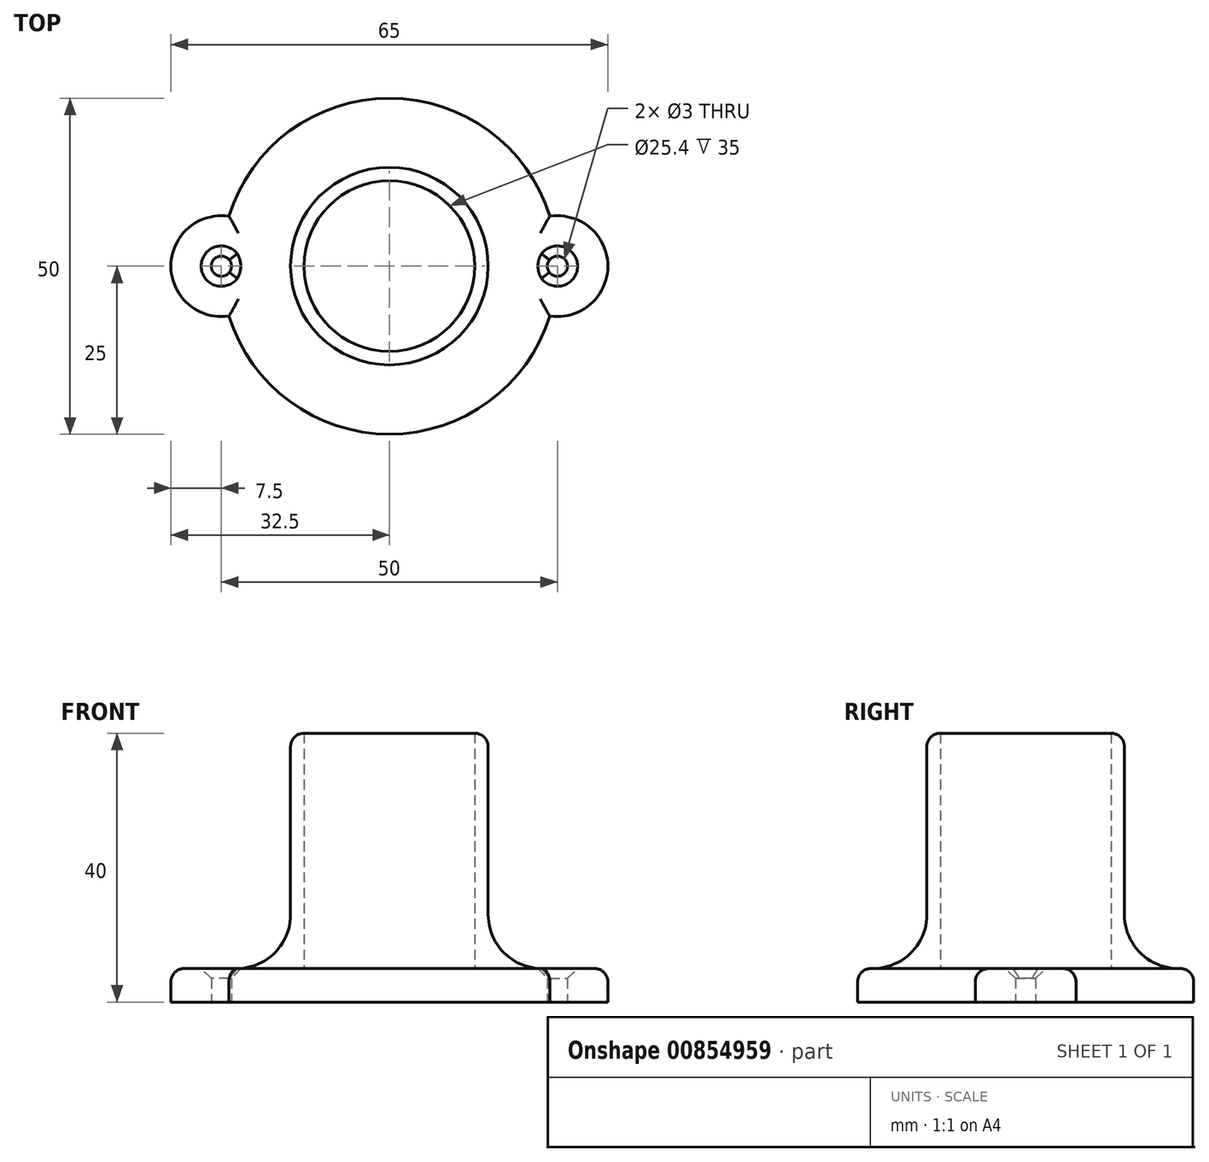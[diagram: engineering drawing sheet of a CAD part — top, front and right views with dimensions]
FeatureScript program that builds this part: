
annotation { "Feature Type Name" : "Feature", "Feature Type Description" : "" }
export const myFeature = defineFeature(function(context is Context, id is Id, definition is map)
    precondition{}
    {
        {
            var Q0;
            Q0=qCreatedBy(makeId("Top.planeOp"),FACE);
            var sketch = newSketch(context, id + "F0", { "sketchPlane" : qUnion([Q0])});
            skCircle(sketch, "E0", {"center": v(0, 0) * mm, "radius": 12.7 * mm});
            skCircle(sketch, "E1", {"center": v(0, 0) * mm, "radius": 11 * mm});
            skCircle(sketch, "E2", {"center": v(0, 0) * mm, "radius": 9 * mm});
            skCircle(sketch, "E3", {"center": v(0, 0) * mm, "radius": 14.7 * mm});
            skSolve(sketch);
        }
        {
            var Q0;
            Q0 = qSketchRegion(id + "F0", true);
            extrude(context, id + "F1", {"entities" : qUnion([Q0]), "depth" : 40 * mm, "offsetDistance" : 25 * mm});
        }
        {
            var Q0;
            Q0=qCreatedBy(makeId("Top.planeOp"),FACE);
            var sketch = newSketch(context, id + "F2", { "sketchPlane" : qUnion([Q0])});
            skCircle(sketch, "E4", {"center": v(0.24, -0.03) * mm, "radius": 11 * mm});
            skCircle(sketch, "E5", {"center": v(0.24, -0.03) * mm, "radius": 9 * mm});
            skSolve(sketch);
        }
        {
            var Q0;
            Q0=qCreatedBy(makeId("Top.planeOp"),FACE);
            var sketch = newSketch(context, id + "F3", { "sketchPlane" : qUnion([Q0])});
            skArc(sketch, "E6", {"start": v(-23.88, -7.42) * mm, "mid": v(0, -25) * mm, "end": v(23.88, -7.42) * mm});
            skArc(sketch, "E7", {"start": v(-23.88, 7.42) * mm, "mid": v(-32.5, 0) * mm, "end": v(-23.88, -7.42) * mm});
            skArc(sketch, "E8", {"start": v(23.88, -7.42) * mm, "mid": v(32.5, 0) * mm, "end": v(23.88, 7.42) * mm});
            skArc(sketch, "E9.trimOffspring", {"start": v(23.88, 7.42) * mm, "mid": v(0, 25) * mm, "end": v(-23.88, 7.42) * mm});
            skCircle(sketch, "E10", {"center": v(-25, 0) * mm, "radius": 1.5 * mm});
            skCircle(sketch, "E11", {"center": v(25, 0) * mm, "radius": 1.5 * mm});
            skSolve(sketch);
        }
        {
            var Q0;
            Q0 = qSketchRegion(id + "F3", true);
            extrude(context, id + "F4", {"entities" : qUnion([Q0]), "depth" : 5 * mm, "offsetDistance" : 25 * mm});
        }
        {
            var Q0;
            Q0=makeQuery(id+"F1.opExtrude","CAP_EDGE",EDGE,{"disambiguationData":[OSD([sQuery(id+"F0.wireOp",EDGE,"E3")])],"isStart":false});
            fillet(context, id + "F5", {"entities" : qUnion([Q0]), "radius" : 2 * mm, "tangentPropagation" : true, "allowEdgeOverflow" : false});
        }
        {
            var Q0;
            Q0=makeQuery(id+"F1.opExtrude","SWEPT_BODY",BODY,{"disambiguationData":[OSD([sQuery(id+"F0.wireOp",EDGE,"E0"),sQuery(id+"F0.wireOp",EDGE,"E3")])]});
            var Q1;
            Q1=makeQuery(id+"F3QXxj1bhoaXKLj_1.opExtrude","SWEPT_BODY",BODY,{"disambiguationData":[OSD([sQuery(id+"F2.wireOp",EDGE,"E4"),sQuery(id+"F2.wireOp",EDGE,"E5")])]});
            var Q2;
            Q2=makeQuery(id+"F4.opExtrude","SWEPT_BODY",BODY,{"disambiguationData":[OSD([sQuery(id+"F3.wireOp",EDGE,"E6"),sQuery(id+"F3.wireOp",EDGE,"E7"),sQuery(id+"F3.wireOp",EDGE,"E8"),sQuery(id+"F3.wireOp",EDGE,"E9.trimOffspring"),sQuery(id+"F3.wireOp",EDGE,"E10"),sQuery(id+"F3.wireOp",EDGE,"E11")])]});
            booleanBodies(context, id + "F6", {"operationType" : BooleanOperationType.UNION, "tools" : qUnion([Q0, Q1, Q2])});
        }
        {
            var Q0;
            Q0=makeQuery(id+"F4.opExtrude","CAP_EDGE",EDGE,{"disambiguationData":[OSD([sQuery(id+"F3.wireOp",EDGE,"E6")])],"isStart":false});
            var Q1;
            Q1=makeQuery(id+"F4.opExtrude","CAP_EDGE",EDGE,{"disambiguationData":[OSD([sQuery(id+"F3.wireOp",EDGE,"E9.trimOffspring")])],"isStart":false});
            var Q2;
            Q2=makeQuery(id+"F4.opExtrude","CAP_EDGE",EDGE,{"disambiguationData":[OSD([sQuery(id+"F3.wireOp",EDGE,"E7")])],"isStart":false});
            var Q3;
            Q3=makeQuery(id+"F4.opExtrude","CAP_EDGE",EDGE,{"disambiguationData":[OSD([sQuery(id+"F3.wireOp",EDGE,"E8")])],"isStart":false});
            fillet(context, id + "F7", {"entities" : qUnion([Q0, Q1, Q2, Q3]), "radius" : 2 * mm, "tangentPropagation" : true, "allowEdgeOverflow" : false});
        }
        {
            var Q0;
            Q0=makeQuery(id+"F6.opBoolean","INTERSECT",EDGE,{"derivedFrom":[makeQuery(id+"F4.opExtrude","CAP_FACE",FACE,{"disambiguationData":[OSD([sQuery(id+"F3.wireOp",EDGE,"E6"),sQuery(id+"F3.wireOp",EDGE,"E7"),sQuery(id+"F3.wireOp",EDGE,"E8"),sQuery(id+"F3.wireOp",EDGE,"E9.trimOffspring"),sQuery(id+"F3.wireOp",EDGE,"E10"),sQuery(id+"F3.wireOp",EDGE,"E11")])],"isStart":false}),makeQuery(id+"F1.opExtrude","SWEPT_FACE",FACE,{"disambiguationData":[OSD([sQuery(id+"F0.wireOp",EDGE,"E3")])]})]});
            fillet(context, id + "F8", {"entities" : qUnion([Q0]), "radius" : 8 * mm, "tangentPropagation" : true, "allowEdgeOverflow" : false});
        }
        {
            var Q0;
            Q0=makeQuery(id+"F4.opExtrude","CAP_EDGE",EDGE,{"disambiguationData":[OSD([sQuery(id+"F3.wireOp",EDGE,"E11")])],"isStart":false});
            var Q1;
            Q1=makeQuery(id+"F4.opExtrude","CAP_EDGE",EDGE,{"disambiguationData":[OSD([sQuery(id+"F3.wireOp",EDGE,"E10")])],"isStart":false});
            chamfer(context, id + "F9", {"entities" : qUnion([Q0, Q1]), "width" : 1.5 * mm, "tangentPropagation" : true});
        }
    });
